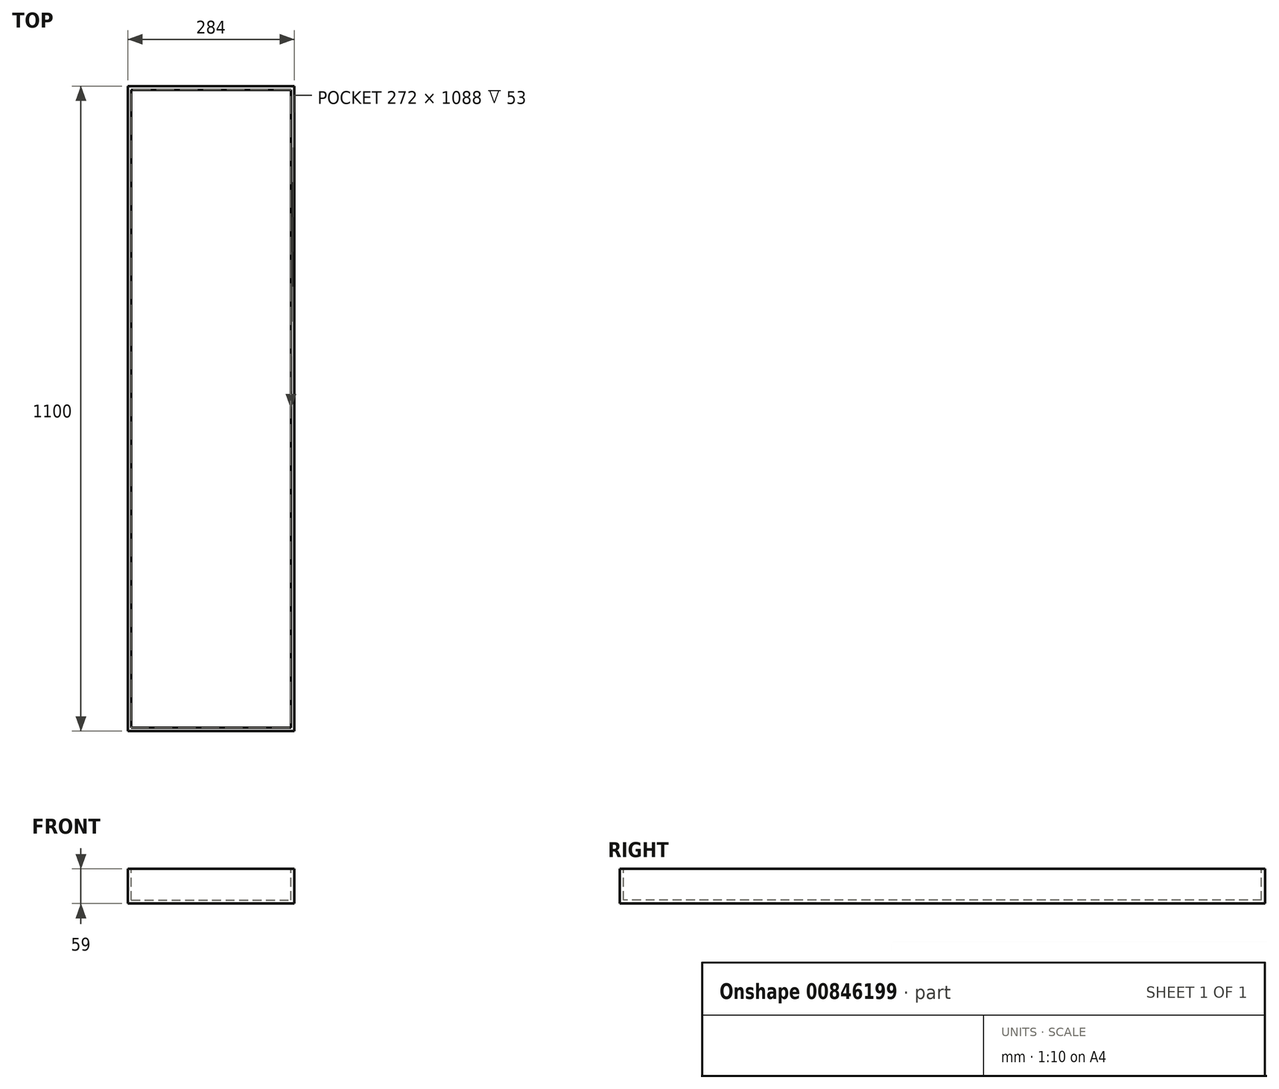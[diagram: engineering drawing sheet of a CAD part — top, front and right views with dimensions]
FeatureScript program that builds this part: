
annotation { "Feature Type Name" : "Feature", "Feature Type Description" : "" }
export const myFeature = defineFeature(function(context is Context, id is Id, definition is map)
    precondition{}
    {
        {
            var Q0;
            Q0=qCreatedBy(makeId("Front.planeOp"),FACE);
            var sketch = newSketch(context, id + "F0", { "sketchPlane" : qUnion([Q0])});
            skLineSegment(sketch, "E0.bottom", {"start": v(-142, 29.5) * mm, "end": v(142, 29.5) * mm});
            skLineSegment(sketch, "E0.top", {"start": v(-142, -29.5) * mm, "end": v(142, -29.5) * mm});
            skLineSegment(sketch, "E0.left", {"start": v(-142, 29.5) * mm, "end": v(-142, -29.5) * mm});
            skLineSegment(sketch, "E0.right", {"start": v(142, 29.5) * mm, "end": v(142, -29.5) * mm});
            skPoint(sketch, "E0.middle", {"position": v(0, 0) * mm});
            skSolve(sketch);
        }
        {
            var Q0;
            Q0=qSketchRegion(id+"F0",true);
            extrude(context, id + "F1", {"entities" : qUnion([Q0]), "depth" : 1100 * mm, "offsetDistance" : 25 * mm});
        }
        {
            var Q0;
            Q0=makeQuery(id+"F1.opExtrude","SWEPT_FACE",FACE,{"disambiguationData":[OSD([sQuery(id+"F0.wireOp",EDGE,"E0.bottom")])]});
            var sketch = newSketch(context, id + "F2", { "sketchPlane" : qUnion([Q0])});
            skLineSegment(sketch, "E1.bottom", {"start": v(-136, 6) * mm, "end": v(148, 6) * mm});
            skLineSegment(sketch, "E1.top", {"start": v(-136, -1094) * mm, "end": v(148, -1094) * mm});
            skLineSegment(sketch, "E1.left", {"start": v(-136, 6) * mm, "end": v(-136, -1094) * mm});
            skLineSegment(sketch, "E1.right", {"start": v(148, 6) * mm, "end": v(148, -1094) * mm});
            skSolve(sketch);
        }
        {
            var Q0;
            Q0=makeQuery(id+"F2.imprint","IMPRINT",FACE,{"disambiguationData":[TD([[makeQuery(id+"F2.imprint","IMPRINT",EDGE,{"derivedFrom":sQuery(id+"F2.wireOp",EDGE,"E1.bottom")}),-1.0]])]});
            extrude(context, id + "F3", {"entities" : qUnion([Q0]), "operationType" : NewBodyOperationType.REMOVE, "oppositeDirection" : true, "depth" : 59 * mm, "offsetDistance" : 25 * mm});
        }
        {
            var Q0;
            Q0=makeQuery(id+"F1.opExtrude","SWEPT_FACE",FACE,{"disambiguationData":[OSD([sQuery(id+"F0.wireOp",EDGE,"E0.bottom")])]});
            var sketch = newSketch(context, id + "F4", { "sketchPlane" : qUnion([Q0])});
            skLineSegment(sketch, "E2.bottom", {"start": v(-136, -6) * mm, "end": v(136, -6) * mm});
            skLineSegment(sketch, "E2.top", {"start": v(-136, -1094) * mm, "end": v(136, -1094) * mm});
            skLineSegment(sketch, "E2.left", {"start": v(-136, -6) * mm, "end": v(-136, -1094) * mm});
            skLineSegment(sketch, "E2.right", {"start": v(136, -6) * mm, "end": v(136, -1094) * mm});
            skSolve(sketch);
        }
        {
            var Q0;
            Q0 = qSketchRegion(id + "F4", true);
            extrude(context, id + "F5", {"entities" : qUnion([Q0]), "operationType" : NewBodyOperationType.REMOVE, "oppositeDirection" : true, "depth" : 53 * mm, "offsetDistance" : 25 * mm});
        }
    });
